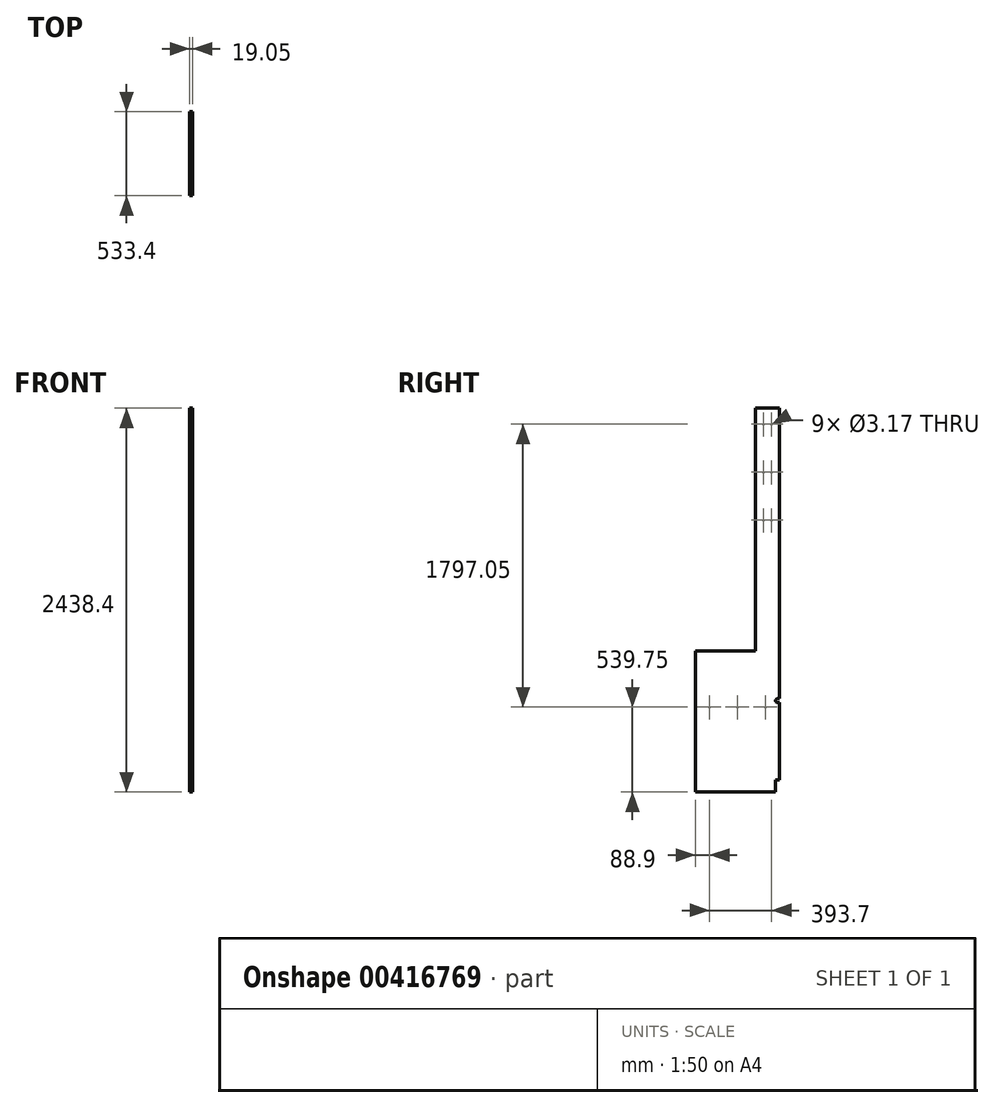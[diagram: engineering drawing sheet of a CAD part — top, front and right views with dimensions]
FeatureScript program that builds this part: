
annotation { "Feature Type Name" : "Feature", "Feature Type Description" : "" }
export const myFeature = defineFeature(function(context is Context, id is Id, definition is map)
    precondition{}
    {
        {
            var Q0;
            Q0=qCreatedBy(makeId("Right.planeOp"),FACE);
            var sketch = newSketch(context, id + "F0", { "sketchPlane" : qUnion([Q0])});
            skLineSegment(sketch, "E0", {"start": v(0, 0) * mm, "end": v(508, 0) * mm});
            skLineSegment(sketch, "E1", {"start": v(508, 0) * mm, "end": v(508, 76.2) * mm});
            skLineSegment(sketch, "E2", {"start": v(508, 76.2) * mm, "end": v(533.4, 76.2) * mm});
            skLineSegment(sketch, "E3", {"start": v(533.4, 76.2) * mm, "end": v(533.4, 2438.4) * mm});
            skLineSegment(sketch, "E4", {"start": v(533.4, 2438.4) * mm, "end": v(381, 2438.4) * mm});
            skLineSegment(sketch, "E5", {"start": v(381, 2438.4) * mm, "end": v(381, 895.35) * mm});
            skLineSegment(sketch, "E6", {"start": v(381, 895.35) * mm, "end": v(0, 895.35) * mm});
            skLineSegment(sketch, "E7", {"start": v(0, 895.35) * mm, "end": v(0, 0) * mm});
            skSolve(sketch);
        }
        {
            var Q0;
            Q0 = qSketchRegion(id + "F0", true);
            extrude(context, id + "F1", {"entities" : qUnion([Q0]), "depth" : 19.05 * mm});
        }
        {
            var Q0;
            Q0=makeQuery(id+"F1.opExtrude","CAP_FACE",FACE,{"disambiguationData":[OSD([sQuery(id+"F0.wireOp",EDGE,"E0"),sQuery(id+"F0.wireOp",EDGE,"E1"),sQuery(id+"F0.wireOp",EDGE,"E2"),sQuery(id+"F0.wireOp",EDGE,"E3"),sQuery(id+"F0.wireOp",EDGE,"E4"),sQuery(id+"F0.wireOp",EDGE,"E5"),sQuery(id+"F0.wireOp",EDGE,"E6"),sQuery(id+"F0.wireOp",EDGE,"E7")])],"isStart":false});
            var sketch = newSketch(context, id + "F2", { "sketchPlane" : qUnion([Q0])});
            skCircle(sketch, "E8", {"center": v(431.8, 2336.8) * mm, "radius": 1.59 * mm});
            skCircle(sketch, "E9", {"center": v(482.6, 2336.8) * mm, "radius": 1.59 * mm});
            skCircle(sketch, "E10", {"center": v(431.8, 2032) * mm, "radius": 1.59 * mm});
            skCircle(sketch, "E11", {"center": v(482.6, 2032) * mm, "radius": 1.59 * mm});
            skCircle(sketch, "E12", {"center": v(431.8, 1727.2) * mm, "radius": 1.59 * mm});
            skCircle(sketch, "E13", {"center": v(482.6, 1727.2) * mm, "radius": 1.59 * mm});
            skLineSegment(sketch, "E14", {"start": v(381, 2336.8) * mm, "end": v(533.4, 2336.8) * mm, "construction": true});
            skLineSegment(sketch, "E15", {"start": v(381, 2032) * mm, "end": v(533.4, 2032) * mm, "construction": true});
            skLineSegment(sketch, "E16", {"start": v(381, 1727.2) * mm, "end": v(533.4, 1727.2) * mm, "construction": true});
            skLineSegment(sketch, "E17", {"start": v(0, 539.75) * mm, "end": v(533.4, 539.75) * mm, "construction": true});
            skCircle(sketch, "E18", {"center": v(88.9, 539.75) * mm, "radius": 1.59 * mm});
            skCircle(sketch, "E19", {"center": v(266.7, 539.75) * mm, "radius": 1.59 * mm});
            skCircle(sketch, "E20", {"center": v(444.5, 539.75) * mm, "radius": 1.59 * mm});
            skLineSegment(sketch, "E21", {"start": v(533.4, 539.75) * mm, "end": v(533.4, 568.33) * mm, "construction": true});
            skLineSegment(sketch, "E22", {"start": v(533.4, 568.33) * mm, "end": v(533.4, 581.03) * mm, "construction": true});
            skLineSegment(sketch, "E23", {"start": v(533.4, 581.03) * mm, "end": v(520.7, 581.03) * mm, "construction": true});
            skArc(sketch, "E24", {"start": v(520.7, 593.73) * mm, "mid": v(508, 581.03) * mm, "end": v(520.7, 568.33) * mm});
            skLineSegment(sketch, "E25", {"start": v(520.7, 593.73) * mm, "end": v(533.4, 593.73) * mm});
            skLineSegment(sketch, "E26", {"start": v(520.7, 568.33) * mm, "end": v(533.4, 568.33) * mm});
            skLineSegment(sketch, "E27", {"start": v(533.4, 568.33) * mm, "end": v(533.4, 593.73) * mm});
            skSolve(sketch);
        }
        {
            var Q0;
            Q0 = qSketchRegion(id + "F2", true);
            extrude(context, id + "F3", {"entities" : qUnion([Q0]), "operationType" : NewBodyOperationType.REMOVE, "oppositeDirection" : true, "depth" : 25.4 * mm});
        }
    });
